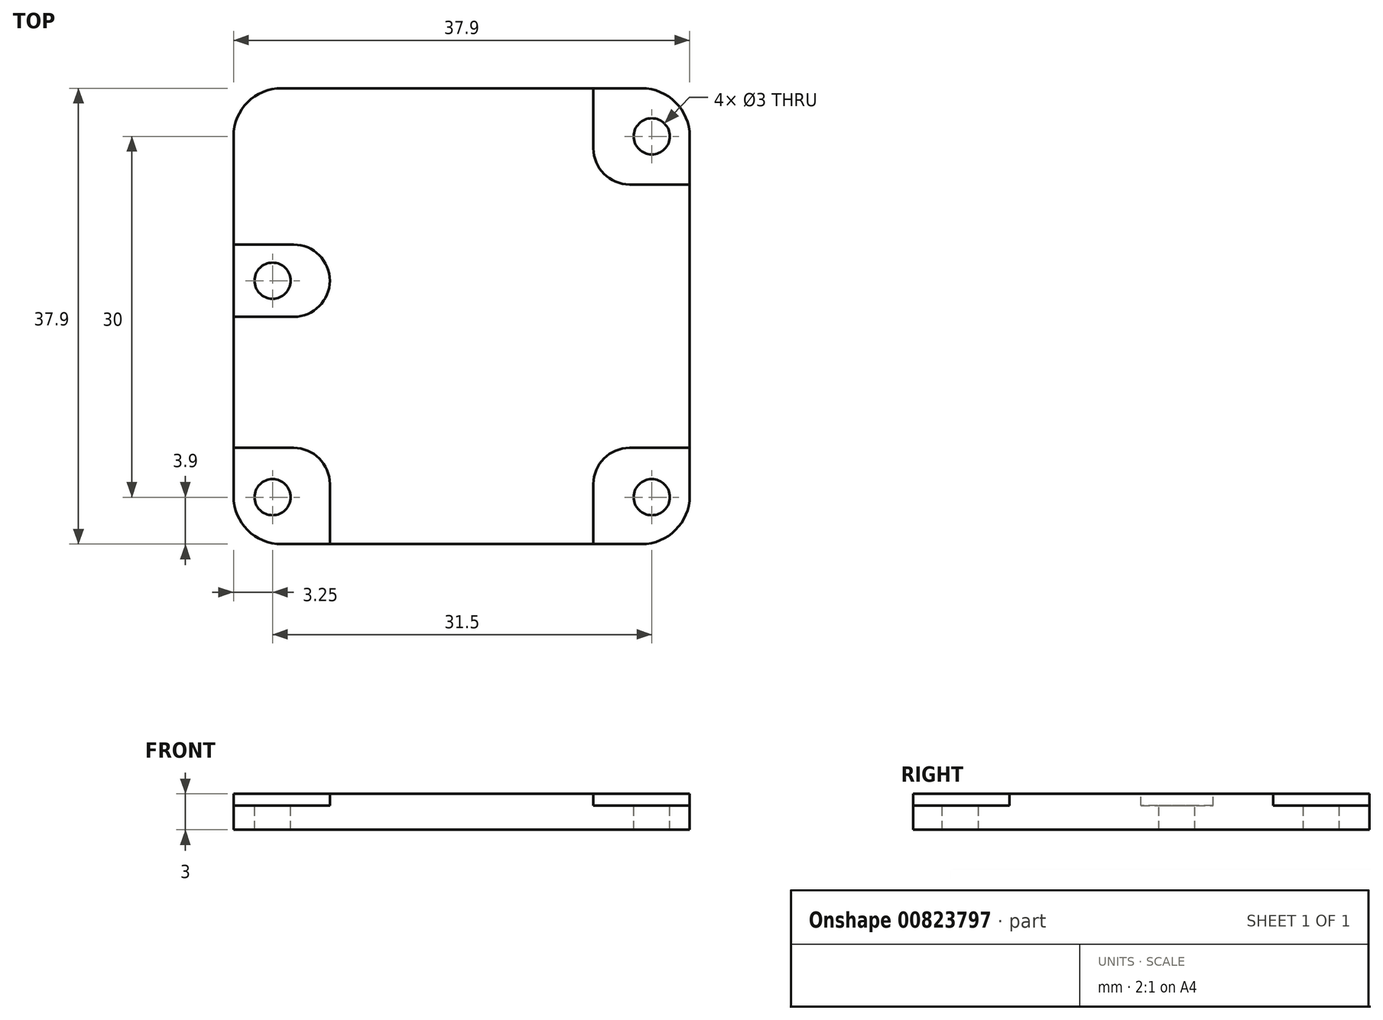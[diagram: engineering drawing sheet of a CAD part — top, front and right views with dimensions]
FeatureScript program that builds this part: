
annotation { "Feature Type Name" : "Feature", "Feature Type Description" : "" }
export const myFeature = defineFeature(function(context is Context, id is Id, definition is map)
    precondition{}
    {
        {
            var Q0;
            Q0=qCreatedBy(makeId("Top.planeOp"),FACE);
            var sketch = newSketch(context, id + "F0", { "sketchPlane" : qUnion([Q0])});
            skLineSegment(sketch, "E0.bottom", {"start": v(-15, 19) * mm, "end": v(14.9, 19) * mm});
            skLineSegment(sketch, "E0.top", {"start": v(-15, -18.9) * mm, "end": v(14.9, -18.9) * mm});
            skLineSegment(sketch, "E0.left", {"start": v(-19, 15) * mm, "end": v(-19, -14.9) * mm});
            skLineSegment(sketch, "E0.right", {"start": v(18.9, 15) * mm, "end": v(18.9, -14.9) * mm});
            skPoint(sketch, "E1.visualSharp", {"position": v(-19, 19) * mm});
            skArc(sketch, "E1.filletArc", {"start": v(-15, 19) * mm, "mid": v(-17.83, 17.83) * mm, "end": v(-19, 15) * mm});
            skPoint(sketch, "E2.visualSharp", {"position": v(-19, -18.9) * mm});
            skArc(sketch, "E2.filletArc", {"start": v(-19, -14.9) * mm, "mid": v(-17.83, -17.73) * mm, "end": v(-15, -18.9) * mm});
            skPoint(sketch, "E3.visualSharp", {"position": v(18.9, -18.9) * mm});
            skArc(sketch, "E3.filletArc", {"start": v(14.9, -18.9) * mm, "mid": v(17.73, -17.73) * mm, "end": v(18.9, -14.9) * mm});
            skPoint(sketch, "E4.visualSharp", {"position": v(18.9, 19) * mm});
            skArc(sketch, "E4.filletArc", {"start": v(18.9, 15) * mm, "mid": v(17.73, 17.83) * mm, "end": v(14.9, 19) * mm});
            skSolve(sketch);
        }
        {
            var Q0;
            Q0=makeQuery(id+"F0.imprint","IMPRINT",FACE,{"disambiguationData":[TD([[makeQuery(id+"F0.imprint","IMPRINT",EDGE,{"derivedFrom":sQuery(id+"F0.wireOp",EDGE,"E0.bottom")}),-1.0]])]});
            extrude(context, id + "F1", {"entities" : qUnion([Q0]), "depth" : 3 * mm, "offsetDistance" : 25 * mm});
        }
        {
            var Q0;
            Q0=makeQuery(id+"F1.opExtrude","CAP_FACE",FACE,{"disambiguationData":[OSD([sQuery(id+"F0.wireOp",EDGE,"E0.bottom"),sQuery(id+"F0.wireOp",EDGE,"E0.top"),sQuery(id+"F0.wireOp",EDGE,"E0.left"),sQuery(id+"F0.wireOp",EDGE,"E0.right"),sQuery(id+"F0.wireOp",EDGE,"E1.filletArc"),sQuery(id+"F0.wireOp",EDGE,"E2.filletArc"),sQuery(id+"F0.wireOp",EDGE,"E3.filletArc"),sQuery(id+"F0.wireOp",EDGE,"E4.filletArc")])],"isStart":false});
            var sketch = newSketch(context, id + "F2", { "sketchPlane" : qUnion([Q0])});
            skLineSegment(sketch, "E5.bottom", {"start": v(-19, 6) * mm, "end": v(-14, 6) * mm});
            skLineSegment(sketch, "E5.top", {"start": v(-19, 0) * mm, "end": v(-14, 0) * mm});
            skLineSegment(sketch, "E5.left", {"start": v(-19, 6) * mm, "end": v(-19, 0) * mm});
            skLineSegment(sketch, "E5.right", {"start": v(-11, 3) * mm, "end": v(-11, 3) * mm});
            skLineSegment(sketch, "E6.bottom", {"start": v(10.9, 19) * mm, "end": v(18.9, 19) * mm});
            skLineSegment(sketch, "E6.top", {"start": v(13.9, 11) * mm, "end": v(18.9, 11) * mm});
            skLineSegment(sketch, "E6.left", {"start": v(10.9, 19) * mm, "end": v(10.9, 14) * mm});
            skLineSegment(sketch, "E6.right", {"start": v(18.9, 19) * mm, "end": v(18.9, 11) * mm});
            skLineSegment(sketch, "E7.bottom", {"start": v(-19, -10.9) * mm, "end": v(-14, -10.9) * mm});
            skLineSegment(sketch, "E7.top", {"start": v(-19, -18.9) * mm, "end": v(-11, -18.9) * mm});
            skLineSegment(sketch, "E7.left", {"start": v(-19, -10.9) * mm, "end": v(-19, -18.9) * mm});
            skLineSegment(sketch, "E7.right", {"start": v(-11, -13.9) * mm, "end": v(-11, -18.9) * mm});
            skLineSegment(sketch, "E8.bottom", {"start": v(18.9, -10.9) * mm, "end": v(13.9, -10.9) * mm});
            skLineSegment(sketch, "E8.top", {"start": v(18.9, -18.9) * mm, "end": v(10.9, -18.9) * mm});
            skLineSegment(sketch, "E8.left", {"start": v(18.9, -10.9) * mm, "end": v(18.9, -18.9) * mm});
            skLineSegment(sketch, "E8.right", {"start": v(10.9, -13.9) * mm, "end": v(10.9, -18.9) * mm});
            skPoint(sketch, "E9.visualSharp", {"position": v(-11, 6) * mm});
            skArc(sketch, "E9.filletArc", {"start": v(-11, 3) * mm, "mid": v(-11.88, 5.12) * mm, "end": v(-14, 6) * mm});
            skPoint(sketch, "E10.visualSharp", {"position": v(-11, 0) * mm});
            skArc(sketch, "E10.filletArc", {"start": v(-14, 0) * mm, "mid": v(-11.88, 0.88) * mm, "end": v(-11, 3) * mm});
            skPoint(sketch, "E11.visualSharp", {"position": v(-11, -10.9) * mm});
            skArc(sketch, "E11.filletArc", {"start": v(-11, -13.9) * mm, "mid": v(-11.88, -11.78) * mm, "end": v(-14, -10.9) * mm});
            skPoint(sketch, "E12.visualSharp", {"position": v(10.9, -10.9) * mm});
            skArc(sketch, "E12.filletArc", {"start": v(13.9, -10.9) * mm, "mid": v(11.78, -11.78) * mm, "end": v(10.9, -13.9) * mm});
            skPoint(sketch, "E13.visualSharp", {"position": v(10.9, 11) * mm});
            skArc(sketch, "E13.filletArc", {"start": v(10.9, 14) * mm, "mid": v(11.78, 11.88) * mm, "end": v(13.9, 11) * mm});
            skSolve(sketch);
        }
        {
            var Q0;
            Q0 = qSketchRegion(id + "F2", true);
            extrude(context, id + "F3", {"entities" : qUnion([Q0]), "operationType" : NewBodyOperationType.REMOVE, "oppositeDirection" : true, "depth" : 1 * mm, "offsetDistance" : 25 * mm});
        }
        {
            var Q0;
            Q0=makeQuery(id+"F3.boolean.opBoolean","COPY",FACE,{"derivedFrom":makeQuery(id+"F3.opExtrude","CAP_FACE",FACE,{"disambiguationData":[OSD([sQuery(id+"F2.wireOp",EDGE,"E5.bottom"),sQuery(id+"F2.wireOp",EDGE,"E5.top"),sQuery(id+"F2.wireOp",EDGE,"E5.left"),sQuery(id+"F2.wireOp",EDGE,"E5.right"),sQuery(id+"F2.wireOp",EDGE,"E9.filletArc"),sQuery(id+"F2.wireOp",EDGE,"E10.filletArc")])],"isStart":false})});
            var sketch = newSketch(context, id + "F4", { "sketchPlane" : qUnion([Q0])});
            skCircle(sketch, "E14", {"center": v(-15.75, 3) * mm, "radius": 1.5 * mm});
            skCircle(sketch, "E15", {"center": v(15.75, 15) * mm, "radius": 1.5 * mm});
            skCircle(sketch, "E16", {"center": v(15.75, -15) * mm, "radius": 1.5 * mm});
            skCircle(sketch, "E17", {"center": v(-15.75, -15) * mm, "radius": 1.5 * mm});
            skSolve(sketch);
        }
        {
            var Q0;
            Q0 = qSketchRegion(id + "F4", true);
            extrude(context, id + "F5", {"entities" : qUnion([Q0]), "operationType" : NewBodyOperationType.REMOVE, "oppositeDirection" : true, "depth" : 25 * mm, "offsetDistance" : 25 * mm});
        }
    });
